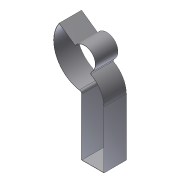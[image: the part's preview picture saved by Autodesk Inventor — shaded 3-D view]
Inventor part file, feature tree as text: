
AUTODESK INVENTOR PART (.ipt)
format: ipt  version: 2012 (Build 160160000, 160)  size: 118,272 bytes
history: native  units: in
note: dims shown in document units (in); Inventor stores cm internally (conversion verified against a paired STEP export)
features: extrude x1, shell x1, sketch x1
ambient origin geometry x8: Origin, YZ Plane, XZ Plane, XY Plane, X Axis, Y Axis, Z Axis, Center Point
bodies: Solid1 (feature_tree)
feature tree (3):
  extrude  "Extrusion1"  Depth=11.0in
  shell  "Shell1"  Thickness=2.0in
  sketch  "Sketch1"  dims[d0=8.0in d1=11.0in d3=2.0in d4=59.0in d5=27.0in d6=1.5in d9=0.3779in d10=40.5in d11=8.0in d12=0.0in d13=0.1in d14=8.42in d20=12.0in d21=7.0in]
